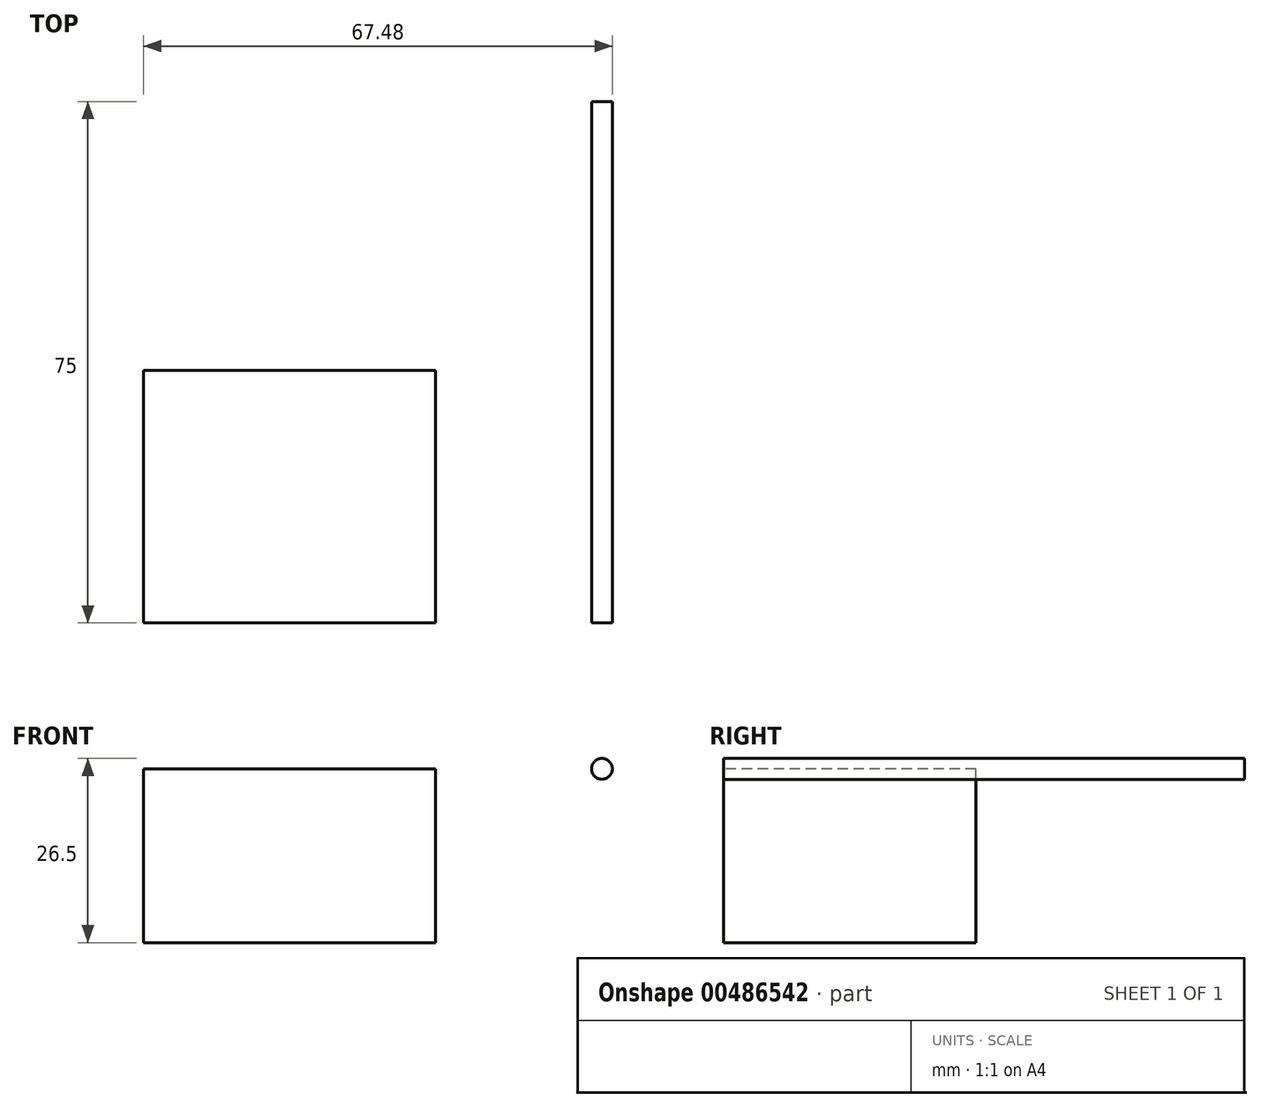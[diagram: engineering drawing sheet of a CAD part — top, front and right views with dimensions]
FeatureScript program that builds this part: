
annotation { "Feature Type Name" : "Feature", "Feature Type Description" : "" }
export const myFeature = defineFeature(function(context is Context, id is Id, definition is map)
    precondition{}
    {
        {
            var Q0;
            Q0=qCreatedBy(makeId("Front.planeOp"),FACE);
            var sketch = newSketch(context, id + "F0", { "sketchPlane" : qUnion([Q0])});
            skCircle(sketch, "E0", {"center": v(0, 0) * mm, "radius": 1.5 * mm});
            skSolve(sketch);
        }
        {
            var Q0;
            Q0 = qSketchRegion(id + "F0", true);
            extrude(context, id + "F1", {"entities" : qUnion([Q0]), "oppositeDirection" : true, "depth" : 75 * mm, "offsetDistance" : 25 * mm});
        }
        {
            var Q0;
            Q0=qCreatedBy(makeId("Top.planeOp"),FACE);
            var sketch = newSketch(context, id + "F2", { "sketchPlane" : qUnion([Q0])});
            skLineSegment(sketch, "E1.bottom", {"start": v(-65.98, 36.32) * mm, "end": v(-23.98, 36.32) * mm});
            skLineSegment(sketch, "E1.top", {"start": v(-65.98, 0) * mm, "end": v(-23.98, 0) * mm});
            skLineSegment(sketch, "E1.left", {"start": v(-65.98, 36.32) * mm, "end": v(-65.98, 0) * mm});
            skLineSegment(sketch, "E1.right", {"start": v(-23.98, 36.32) * mm, "end": v(-23.98, 0) * mm});
            skSolve(sketch);
        }
        {
            var Q0;
            Q0=makeQuery(id+"F2.imprint","IMPRINT",FACE,{"disambiguationData":[TD([[makeQuery(id+"F2.imprint","IMPRINT",EDGE,{"derivedFrom":sQuery(id+"F2.wireOp",EDGE,"E1.bottom")}),-1.0]])]});
            extrude(context, id + "F3", {"entities" : qUnion([Q0]), "oppositeDirection" : true, "depth" : 25 * mm, "offsetDistance" : 25 * mm});
        }
    });
